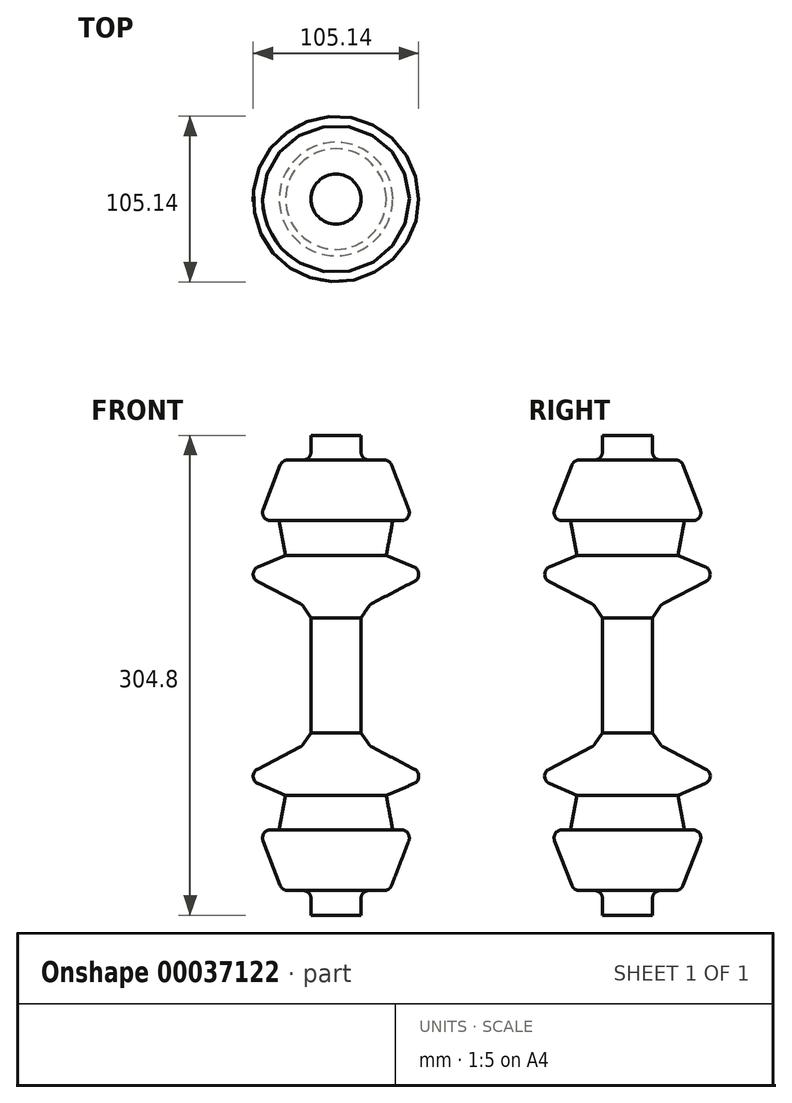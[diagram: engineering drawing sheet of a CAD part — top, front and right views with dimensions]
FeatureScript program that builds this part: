
annotation { "Feature Type Name" : "Feature", "Feature Type Description" : "" }
export const myFeature = defineFeature(function(context is Context, id is Id, definition is map)
    precondition{}
    {
        {
            var Q0;
            Q0=qCreatedBy(makeId("Top.planeOp"),FACE);
            var sketch = newSketch(context, id + "F0", { "sketchPlane" : qUnion([Q0])});
            skCircle(sketch, "E0", {"center": v(0, 0) * mm, "radius": 15.88 * mm});
            skSolve(sketch);
        }
        {
            var Q0;
            Q0 = qSketchRegion(id + "F0", true);
            extrude(context, id + "F1", {"entities" : qUnion([Q0]), "endBound" : BoundingType.SYMMETRIC, "depth" : 152.4 * mm, "hasSecondDirection" : true, "secondDirectionOppositeDirection" : true, "secondDirectionDepth" : 25.4 * mm});
        }
        {
            var Q0;
            Q0=qCreatedBy(makeId("Front.planeOp"),FACE);
            var sketch = newSketch(context, id + "F2", { "sketchPlane" : qUnion([Q0])});
            skLineSegment(sketch, "E1", {"start": v(0, 0) * mm, "end": v(0, -74.37) * mm, "construction": true});
            skSolve(sketch);
        }
        {
            var Q0;
            Q0=qCreatedBy(makeId("Right.planeOp"),FACE);
            var sketch = newSketch(context, id + "F3", { "sketchPlane" : qUnion([Q0])});
            skLineSegment(sketch, "E2", {"start": v(0, 60.5) * mm, "end": v(34.14, 60.5) * mm});
            skLineSegment(sketch, "E3", {"start": v(34.14, 60.5) * mm, "end": v(48.9, 21.96) * mm});
            skLineSegment(sketch, "E4", {"start": v(48.9, 21.96) * mm, "end": v(36.08, 21.96) * mm});
            skLineSegment(sketch, "E5", {"start": v(36.08, 21.96) * mm, "end": v(31.94, 0) * mm});
            skLineSegment(sketch, "E6", {"start": v(31.94, 0) * mm, "end": v(59.44, -11.56) * mm});
            skLineSegment(sketch, "E7", {"start": v(59.44, -11.56) * mm, "end": v(21.77, -31.15) * mm});
            skLineSegment(sketch, "E8", {"start": v(21.77, -31.15) * mm, "end": v(0, -62.79) * mm});
            skLineSegment(sketch, "E9", {"start": v(0, -62.79) * mm, "end": v(0, 60.5) * mm});
            skSolve(sketch);
        }
        {
            var Q0;
            Q0 = qSketchRegion(id + "F3", true);
            var Q1;
            Q1=sQuery(id+"F2.wireOp",EDGE,"E1");
            revolve(context, id + "F4", {"operationType" : NewBodyOperationType.ADD, "entities" : qUnion([Q0]), "axis" : qUnion([Q1]), "revolveType" : RevolveType.FULL});
        }
        {
            var Q0;
            Q0=makeQuery(id+"F4.opRevolve","SWEPT_FACE",FACE,{"disambiguationData":[OSD([sQuery(id+"F3.wireOp",EDGE,"E2")])]});
            var Q1;
            Q1=makeQuery(id+"F4.opRevolve","SWEPT_EDGE",EDGE,{"disambiguationData":[OSD([sQuery(id+"F3.wireOp",EDGE,"E3"),sQuery(id+"F3.wireOp",EDGE,"E4")])]});
            var Q2;
            Q2=makeQuery(id+"F4.opRevolve","SWEPT_EDGE",EDGE,{"disambiguationData":[OSD([sQuery(id+"F3.wireOp",EDGE,"E6"),sQuery(id+"F3.wireOp",EDGE,"E7")])]});
            var Q3;
            Q3=makeQuery(id+"F4.opRevolve","SWEPT_EDGE",EDGE,{"disambiguationData":[OSD([sQuery(id+"F3.wireOp",EDGE,"E7"),sQuery(id+"F3.wireOp",EDGE,"E8")])]});
            fillet(context, id + "F5", {"entities" : qUnion([Q0, Q1, Q2, Q3]), "radius" : 5.08 * mm, "tangentPropagation" : true, "allowEdgeOverflow" : false});
        }
        {
            var Q0;
            Q0=makeQuery(id+"F1.opExtrude","SWEPT_BODY",BODY,{"disambiguationData":[OSD([sQuery(id+"F0.wireOp",EDGE,"E0")])]});
            var Q1;
            Q1=makeQuery(id+"F1.opExtrude","CAP_FACE",FACE,{"disambiguationData":[OSD([sQuery(id+"F0.wireOp",EDGE,"E0")])],"isStart":true});
            mirror(context, id + "F6", {"operationType" : NewBodyOperationType.ADD, "entities" : qUnion([Q0]), "mirrorPlane" : qUnion([Q1])});
        }
    });
